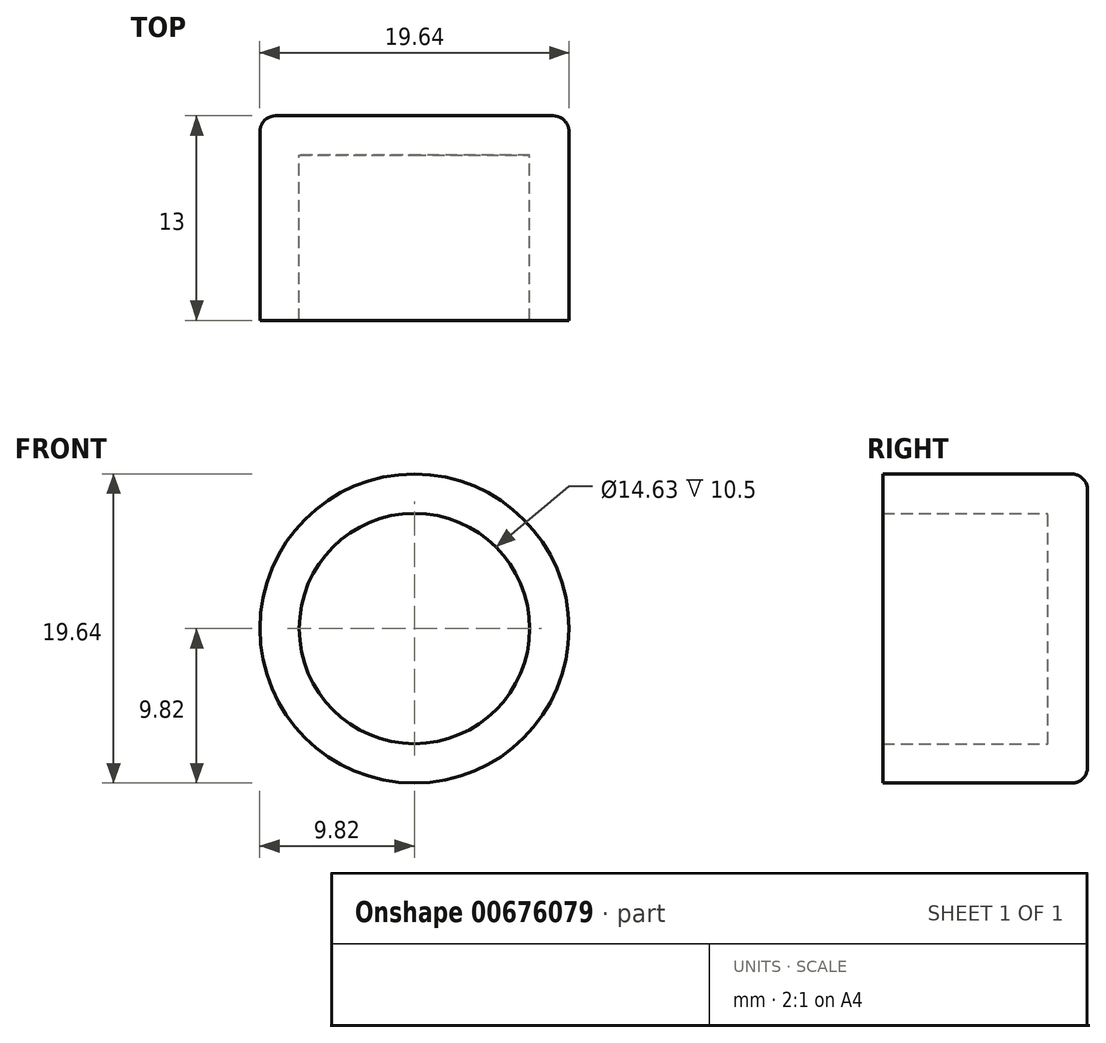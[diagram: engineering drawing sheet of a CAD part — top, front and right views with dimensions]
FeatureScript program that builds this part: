
annotation { "Feature Type Name" : "Feature", "Feature Type Description" : "" }
export const myFeature = defineFeature(function(context is Context, id is Id, definition is map)
    precondition{}
    {
        {
            var Q0;
            Q0=qCreatedBy(makeId("Front.planeOp"),FACE);
            var sketch = newSketch(context, id + "F0", { "sketchPlane" : qUnion([Q0])});
            skCircle(sketch, "E0", {"center": v(0, 0) * mm, "radius": 9.82 * mm});
            skSolve(sketch);
        }
        {
            var Q0;
            Q0 = qSketchRegion(id + "F0", true);
            extrude(context, id + "F1", {"entities" : qUnion([Q0]), "depth" : 13 * mm, "offsetDistance" : 25 * mm});
        }
        {
            var Q0;
            Q0=makeQuery(id+"F1.opExtrude","CAP_EDGE",EDGE,{"disambiguationData":[OSD([sQuery(id+"F0.wireOp",EDGE,"E0")])],"isStart":true});
            fillet(context, id + "F2", {"entities" : qUnion([Q0]), "radius" : 1 * mm, "tangentPropagation" : true, "allowEdgeOverflow" : false});
        }
        {
            var Q0;
            Q0=makeQuery(id+"F1.opExtrude","CAP_FACE",FACE,{"disambiguationData":[OSD([sQuery(id+"F0.wireOp",EDGE,"E0")])],"isStart":false});
            shell(context, id + "F3", {"entities" : qUnion([Q0]), "thickness" : 2.5 * mm});
        }
    });
